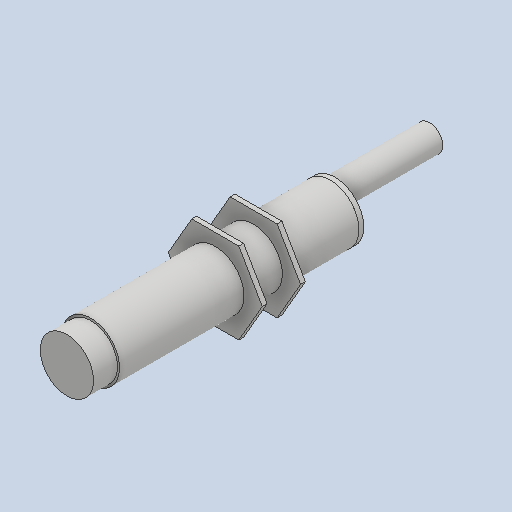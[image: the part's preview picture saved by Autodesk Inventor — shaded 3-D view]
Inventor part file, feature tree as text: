
AUTODESK INVENTOR PART (.ipt)
format: ipt  version: 2023 (Build 270158000, 158)  size: 162,304 bytes
history: native  units: mm
features: other x4, fillet x1
ambient origin geometry x8: Origin, YZ Plane, XZ Plane, XY Plane, X Axis, Y Axis, Z Axis, Center Point
bodies: Solid1 (feature_tree), Solid2 (feature_tree), Solid3 (feature_tree), Solid4 (feature_tree), Solid5 (feature_tree)
feature tree (5):
  other  "Boss-Extrude2"
  other  "Boss-Extrude3"
  other  "Boss-Extrude4"
  fillet  "Fillet1"  [1 undecoded]
  other  "Boss-Extrude7"
note: 1 required parameter value undecoded (feature->parameter linkage not recoverable at this tier; creation-order binding heuristic only, values carry confidence <= 0.55)
